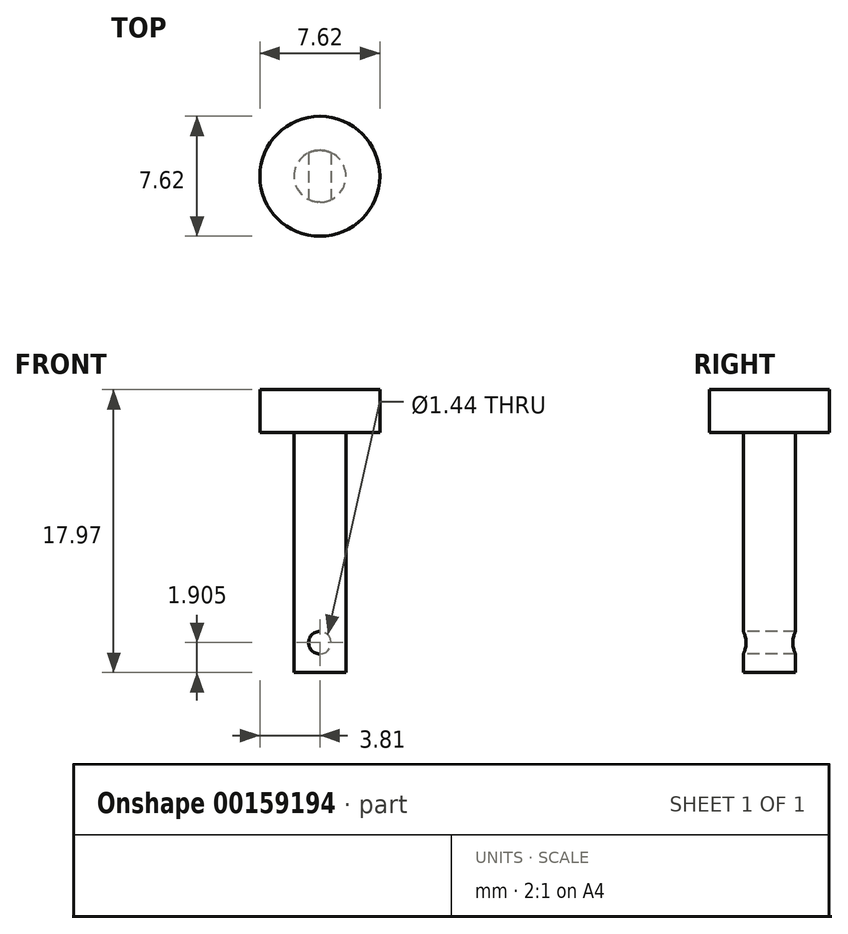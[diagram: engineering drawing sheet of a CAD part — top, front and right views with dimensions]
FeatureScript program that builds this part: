
annotation { "Feature Type Name" : "Feature", "Feature Type Description" : "" }
export const myFeature = defineFeature(function(context is Context, id is Id, definition is map)
    precondition{}
    {
        {
            var Q0;
            Q0=qCreatedBy(makeId("Top.planeOp"),FACE);
            var sketch = newSketch(context, id + "F0", { "sketchPlane" : qUnion([Q0])});
            skCircle(sketch, "E0", {"center": v(0, 0) * mm, "radius": 1.65 * mm});
            skSolve(sketch);
        }
        {
            var Q0;
            Q0=makeQuery(id+"F0.imprint","IMPRINT",FACE,{"disambiguationData":[TD([[makeQuery(id+"F0.imprint","IMPRINT",EDGE,{"derivedFrom":sQuery(id+"F0.wireOp",EDGE,"E0")}),1.0]])]});
            extrude(context, id + "F1", {"entities" : qUnion([Q0]), "depth" : 15.24 * mm});
        }
        {
            var Q0;
            Q0=qCreatedBy(makeId("Front.planeOp"),FACE);
            var sketch = newSketch(context, id + "F2", { "sketchPlane" : qUnion([Q0])});
            skLineSegment(sketch, "E1", {"start": v(0, 15.24) * mm, "end": v(3.8, 15.24) * mm});
            skLineSegment(sketch, "E2", {"start": v(0, 14.39) * mm, "end": v(0, 15.09) * mm, "construction": true});
            skLineSegment(sketch, "E3", {"start": v(0, 15.24) * mm, "end": v(0, 17.97) * mm});
            skPoint(sketch, "E4.orphan", {"position": v(-3.8, 15.24) * mm});
            skLineSegment(sketch, "E5", {"start": v(0, 17.97) * mm, "end": v(3.8, 17.97) * mm});
            skLineSegment(sketch, "E6", {"start": v(3.8, 17.97) * mm, "end": v(3.8, 15.24) * mm});
            skSolve(sketch);
        }
        {
            var Q0;
            Q0 = qSketchRegion(id + "F2", true);
            var Q1;
            Q1=sQuery(id+"F2.wireOp",EDGE,"E3");
            revolve(context, id + "F3", {"operationType" : NewBodyOperationType.ADD, "entities" : qUnion([Q0]), "axis" : qUnion([Q1]), "revolveType" : RevolveType.FULL});
        }
        {
            var Q0;
            Q0=qCreatedBy(makeId("Front.planeOp"),FACE);
            var sketch = newSketch(context, id + "F4", { "sketchPlane" : qUnion([Q0])});
            skCircle(sketch, "E7", {"center": v(0, 1.9) * mm, "radius": 0.72 * mm});
            skSolve(sketch);
        }
        {
            var Q0;
            Q0 = qSketchRegion(id + "F4", true);
            extrude(context, id + "F5", {"entities" : qUnion([Q0]), "operationType" : NewBodyOperationType.REMOVE, "endBound" : BoundingType.THROUGH_ALL, "oppositeDirection" : true, "depth" : 25.4 * mm});
        }
        {
            var Q0;
            Q0 = qSketchRegion(id + "F4", true);
            extrude(context, id + "F6", {"entities" : qUnion([Q0]), "operationType" : NewBodyOperationType.REMOVE, "endBound" : BoundingType.THROUGH_ALL, "depth" : 25.4 * mm});
        }
    });
